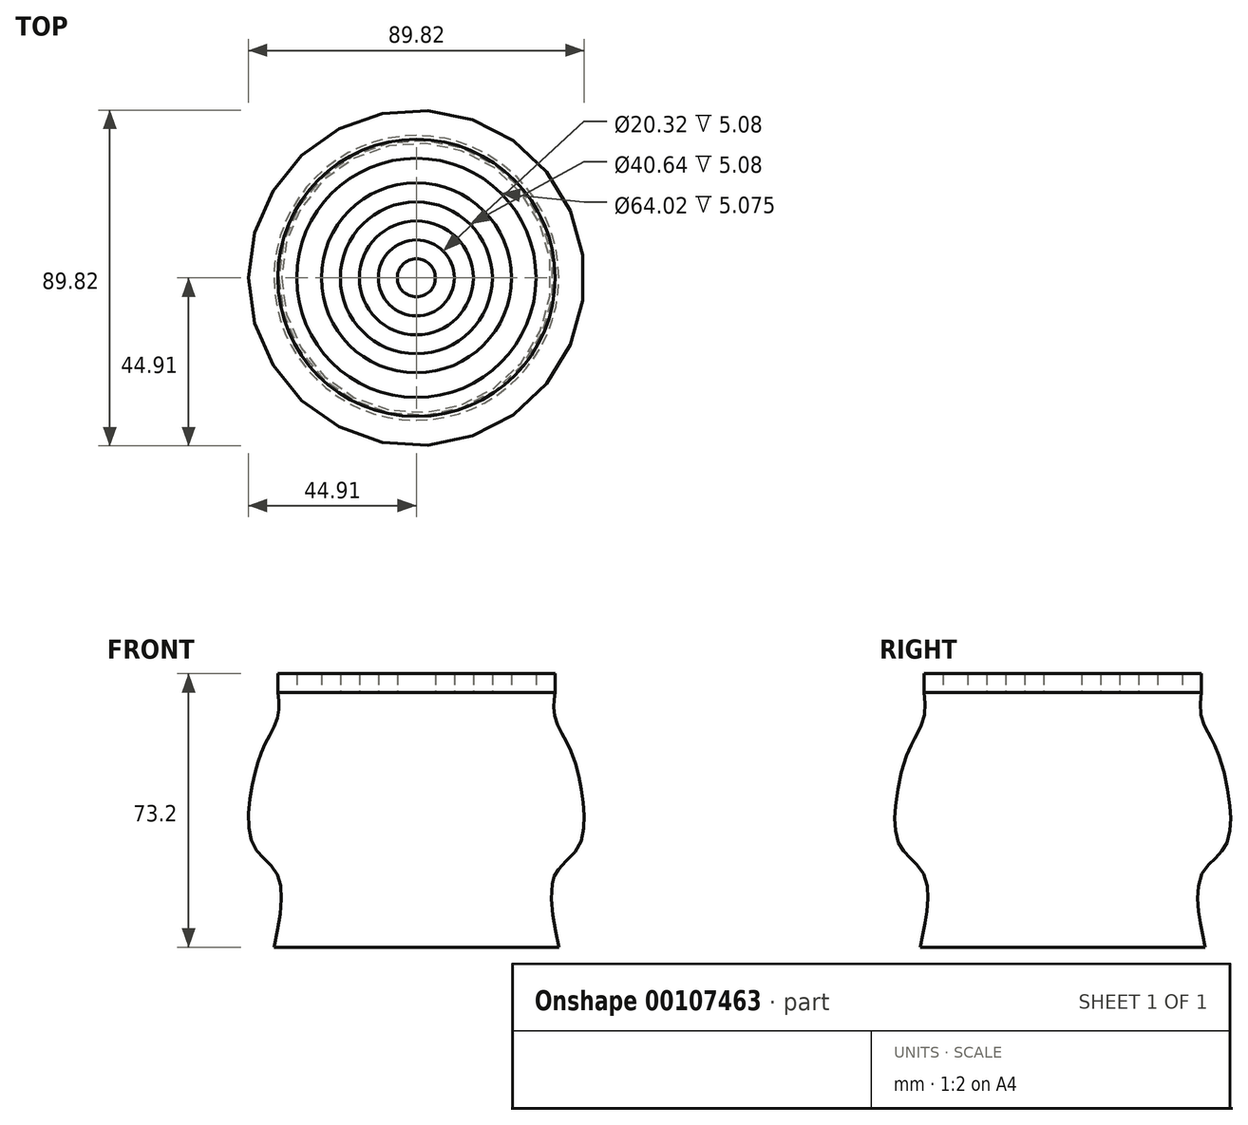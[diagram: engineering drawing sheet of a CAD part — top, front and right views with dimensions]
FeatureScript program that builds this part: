
annotation { "Feature Type Name" : "Feature", "Feature Type Description" : "" }
export const myFeature = defineFeature(function(context is Context, id is Id, definition is map)
    precondition{}
    {
        {
            var Q0;
            Q0=qCreatedBy(makeId("Front.planeOp"),FACE);
            var sketch = newSketch(context, id + "F0", { "sketchPlane" : qUnion([Q0])});
            skLineSegment(sketch, "E0", {"start": v(-38.1, 0) * mm, "end": v(0, 0) * mm});
            skLineSegment(sketch, "E1", {"start": v(0, 0) * mm, "end": v(0, 73.2) * mm});
            skLineSegment(sketch, "E2", {"start": v(0, 73.2) * mm, "end": v(-5.08, 73.2) * mm});
            skLineSegment(sketch, "E3", {"start": v(-5.08, 73.2) * mm, "end": v(-5.08, 68.12) * mm});
            skLineSegment(sketch, "E4", {"start": v(-5.08, 68.12) * mm, "end": v(-10.16, 68.12) * mm});
            skLineSegment(sketch, "E5", {"start": v(-10.16, 68.12) * mm, "end": v(-10.16, 73.2) * mm});
            skLineSegment(sketch, "E6", {"start": v(-10.16, 73.2) * mm, "end": v(-15.24, 73.2) * mm});
            skLineSegment(sketch, "E7", {"start": v(-15.24, 73.2) * mm, "end": v(-15.24, 68.12) * mm});
            skLineSegment(sketch, "E8", {"start": v(-15.24, 68.12) * mm, "end": v(-20.32, 68.12) * mm});
            skLineSegment(sketch, "E9", {"start": v(-20.32, 68.12) * mm, "end": v(-20.32, 73.2) * mm});
            skLineSegment(sketch, "E10", {"start": v(-20.32, 73.2) * mm, "end": v(-25.4, 73.2) * mm});
            skLineSegment(sketch, "E11", {"start": v(-25.4, 73.2) * mm, "end": v(-25.4, 68.12) * mm});
            skLineSegment(sketch, "E12", {"start": v(-25.4, 68.12) * mm, "end": v(-32, 68.12) * mm});
            skLineSegment(sketch, "E13", {"start": v(-32, 68.12) * mm, "end": v(-32, 73.2) * mm});
            skLineSegment(sketch, "E14", {"start": v(-32, 73.2) * mm, "end": v(-37.08, 73.2) * mm});
            skLineSegment(sketch, "E15", {"start": v(-37.08, 73.2) * mm, "end": v(-37.08, 68.12) * mm});
            skFitSpline(sketch, "E16", {"points": [v(-37.08, 68.12) * mm, v(-37.08, 61.48) * mm, v(-40.6, 54.06) * mm, v(-43.72, 44.3) * mm, v(-43.72, 27.52) * mm, v(-37.08, 19.32) * mm, v(-38.1, 0) * mm], "startDerivative": vector(6.6, -52.54) * mm, "endDerivative": vector(-21.45, -103.85) * mm});
            skSolve(sketch);
        }
        {
            var Q0;
            Q0=makeQuery(id+"F0.imprint","IMPRINT",FACE,{"disambiguationData":[TD([[makeQuery(id+"F0.imprint","IMPRINT",EDGE,{"derivedFrom":sQuery(id+"F0.wireOp",EDGE,"E0")}),1.0]])]});
            var Q1;
            Q1=sQuery(id+"F0.wireOp",EDGE,"E1");
            revolve(context, id + "F1", {"entities" : qUnion([Q0]), "axis" : qUnion([Q1]), "revolveType" : RevolveType.FULL});
        }
    });
